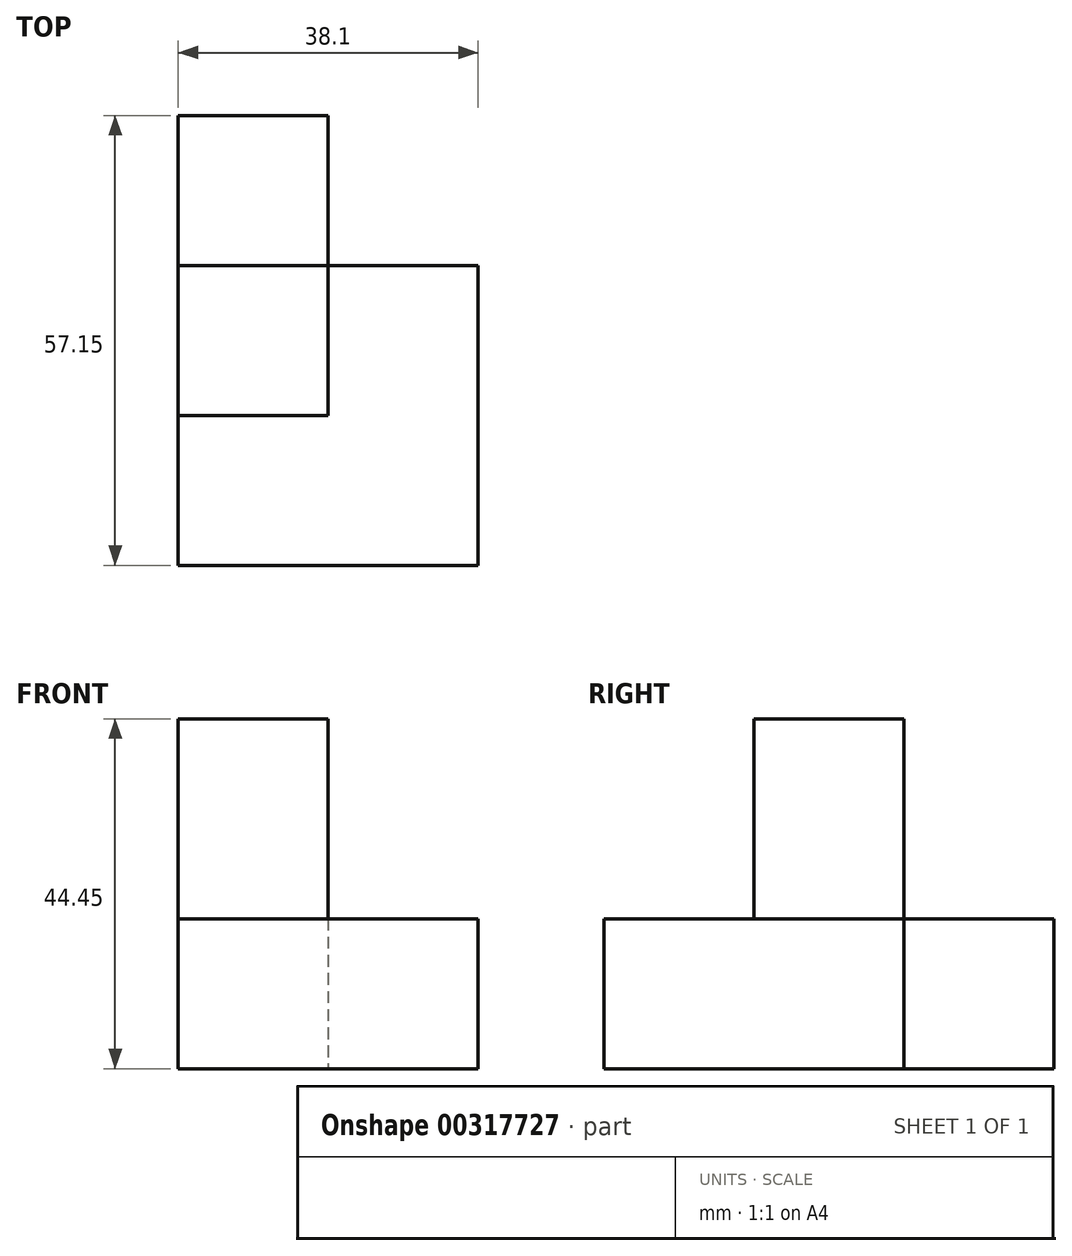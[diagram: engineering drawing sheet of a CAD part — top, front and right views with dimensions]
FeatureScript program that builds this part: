
annotation { "Feature Type Name" : "Feature", "Feature Type Description" : "" }
export const myFeature = defineFeature(function(context is Context, id is Id, definition is map)
    precondition{}
    {
        {
            var Q0;
            Q0=qCreatedBy(makeId("Top.planeOp"),FACE);
            var sketch = newSketch(context, id + "F0", { "sketchPlane" : qUnion([Q0])});
            skLineSegment(sketch, "E0.bottom", {"start": v(0, 0) * mm, "end": v(38.1, 0) * mm});
            skLineSegment(sketch, "E0.top", {"start": v(0, 38.1) * mm, "end": v(38.1, 38.1) * mm});
            skLineSegment(sketch, "E0.left", {"start": v(0, 0) * mm, "end": v(0, 38.1) * mm});
            skLineSegment(sketch, "E0.right", {"start": v(38.1, 0) * mm, "end": v(38.1, 38.1) * mm});
            skLineSegment(sketch, "E1", {"start": v(19.05, 38.1) * mm, "end": v(19.05, 57.15) * mm});
            skLineSegment(sketch, "E2", {"start": v(19.05, 57.15) * mm, "end": v(0, 57.15) * mm});
            skLineSegment(sketch, "E3", {"start": v(0, 57.15) * mm, "end": v(0, 38.1) * mm});
            skSolve(sketch);
        }
        {
            var Q0;
            Q0=makeQuery(id+"F0.imprint","IMPRINT",FACE,{"disambiguationData":[TD([[makeQuery(id+"F0.imprint","IMPRINT",EDGE,{"derivedFrom":sQuery(id+"F0.wireOp",EDGE,"E0.bottom")}),1.0]])]});
            var Q1;
            {var subQ2=sQuery(id+"F0.wireOp",EDGE,"E1");Q1=makeQuery(id+"F0.imprint","IMPRINT",FACE,{"disambiguationData":[TD([[makeQuery(id+"F0.imprint","IMPRINT",EDGE,{"derivedFrom":subQ2}),1.0]])]});}
            extrude(context, id + "F1", {"entities" : qUnion([Q0, Q1]), "depth" : 19.05 * mm});
        }
        {
            var Q0;
            Q0=makeQuery(id+"F1.opExtrude","CAP_FACE",FACE,{"disambiguationData":[OSD([sQuery(id+"F0.wireOp",EDGE,"E0.bottom"),sQuery(id+"F0.wireOp",EDGE,"E0.top"),sQuery(id+"F0.wireOp",EDGE,"E0.left"),sQuery(id+"F0.wireOp",EDGE,"E0.right"),sQuery(id+"F0.wireOp",EDGE,"E1"),sQuery(id+"F0.wireOp",EDGE,"E2"),sQuery(id+"F0.wireOp",EDGE,"E3")])],"isStart":false});
            var sketch = newSketch(context, id + "F2", { "sketchPlane" : qUnion([Q0])});
            skLineSegment(sketch, "E4.bottom", {"start": v(19.05, 38.1) * mm, "end": v(0, 38.1) * mm});
            skLineSegment(sketch, "E4.top", {"start": v(19.05, 19.05) * mm, "end": v(0, 19.05) * mm});
            skLineSegment(sketch, "E4.left", {"start": v(19.05, 38.1) * mm, "end": v(19.05, 19.05) * mm});
            skLineSegment(sketch, "E4.right", {"start": v(0, 38.1) * mm, "end": v(0, 19.05) * mm});
            skSolve(sketch);
        }
        {
            var Q0;
            Q0 = qSketchRegion(id + "F2", true);
            extrude(context, id + "F3", {"entities" : qUnion([Q0]), "operationType" : NewBodyOperationType.ADD, "depth" : 25.4 * mm});
        }
    });
